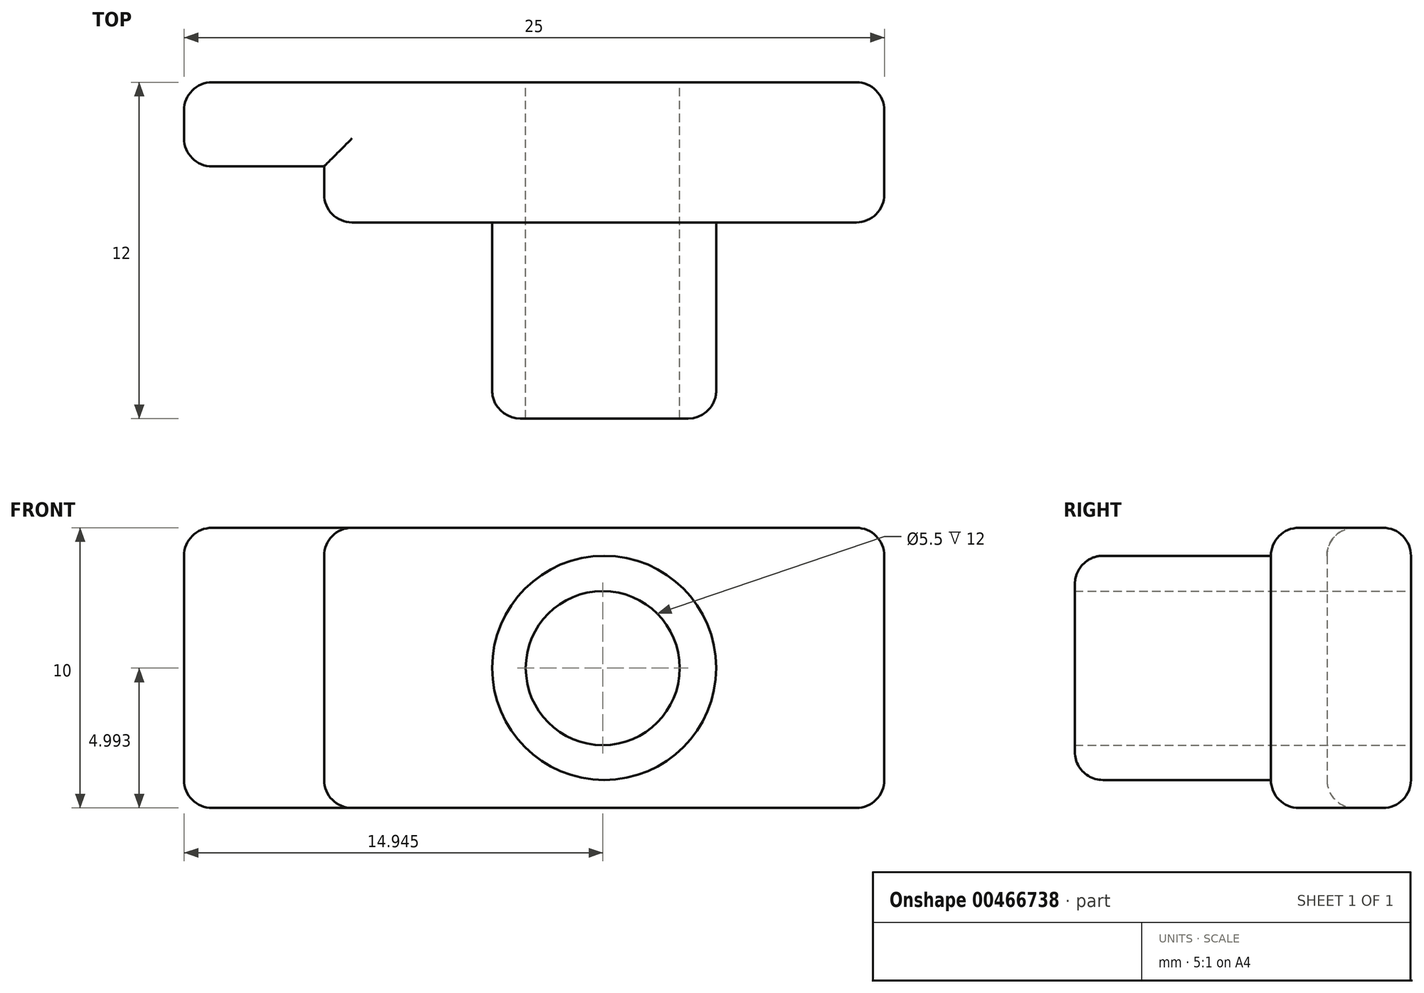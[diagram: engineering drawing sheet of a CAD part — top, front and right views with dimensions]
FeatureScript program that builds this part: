
annotation { "Feature Type Name" : "Feature", "Feature Type Description" : "" }
export const myFeature = defineFeature(function(context is Context, id is Id, definition is map)
    precondition{}
    {
        {
            var Q0;
            Q0=qCreatedBy(makeId("Top.planeOp"),FACE);
            var sketch = newSketch(context, id + "F0", { "sketchPlane" : qUnion([Q0])});
            skLineSegment(sketch, "E0", {"start": v(-34.73, 20.26) * mm, "end": v(-9.73, 20.26) * mm});
            skLineSegment(sketch, "E1", {"start": v(-9.73, 20.26) * mm, "end": v(-9.73, 15.26) * mm});
            skLineSegment(sketch, "E2", {"start": v(-9.73, 15.26) * mm, "end": v(-29.73, 15.26) * mm});
            skLineSegment(sketch, "E3", {"start": v(-29.73, 15.26) * mm, "end": v(-29.73, 17.26) * mm});
            skLineSegment(sketch, "E4", {"start": v(-29.73, 17.26) * mm, "end": v(-34.73, 17.26) * mm});
            skLineSegment(sketch, "E5", {"start": v(-34.73, 17.26) * mm, "end": v(-34.73, 20.26) * mm});
            skSolve(sketch);
        }
        {
            var Q0;
            Q0=makeQuery(id+"F0.imprint","IMPRINT",FACE,{"disambiguationData":[TD([[makeQuery(id+"F0.imprint","IMPRINT",EDGE,{"derivedFrom":sQuery(id+"F0.wireOp",EDGE,"E0")}),-1.0]])]});
            extrude(context, id + "F1", {"entities" : qUnion([Q0]), "depth" : 10 * mm, "offsetDistance" : 25 * mm});
        }
        {
            var Q0;
            Q0=makeQuery(id+"F1.opExtrude","SWEPT_FACE",FACE,{"disambiguationData":[OSD([sQuery(id+"F0.wireOp",EDGE,"E2")])]});
            var sketch = newSketch(context, id + "F2", { "sketchPlane" : qUnion([Q0])});
            skLineSegment(sketch, "E6", {"start": v(-29.73, 10) * mm, "end": v(-9.73, 0) * mm});
            skLineSegment(sketch, "E7", {"start": v(-9.73, 10) * mm, "end": v(-29.73, 0) * mm});
            skPoint(sketch, "E8", {"position": v(-19.73, 5) * mm});
            skCircle(sketch, "E9", {"center": v(-19.73, 5) * mm, "radius": 4 * mm});
            skSolve(sketch);
        }
        {
            var Q0;
            {var subQ0=sQuery(id+"F2.wireOp",EDGE,"E7");var subQ1=sQuery(id+"F2.wireOp",EDGE,"E6");var subQ2=makeQuery(id+"F2.imprint","INTERSECT",VERTEX,{"derivedFrom":[subQ1,subQ0]});Q0=makeQuery(id+"F2.imprint","IMPRINT",FACE,{"disambiguationData":[TD([[makeQuery(id+"F2.imprint","IMPRINT",EDGE,{"disambiguationData":[TD([[subQ2,-1.0]])],"derivedFrom":subQ1}),-1.0]])]});}
            var Q1;
            {var subQ0=sQuery(id+"F2.wireOp",EDGE,"E7");var subQ1=sQuery(id+"F2.wireOp",EDGE,"E6");var subQ2=makeQuery(id+"F2.imprint","INTERSECT",VERTEX,{"derivedFrom":[subQ1,subQ0]});Q1=makeQuery(id+"F2.imprint","IMPRINT",FACE,{"disambiguationData":[TD([[makeQuery(id+"F2.imprint","IMPRINT",EDGE,{"disambiguationData":[TD([[subQ2,-1.0]])],"derivedFrom":subQ1}),1.0]])]});}
            var Q2;
            {var subQ0=sQuery(id+"F2.wireOp",EDGE,"E9");var subQ1=sQuery(id+"F2.wireOp",EDGE,"E6");var subQ2=makeQuery(id+"F2.imprint","INTERSECT",VERTEX,{"disambiguationData":[OD(0.0)],"derivedFrom":[subQ1,subQ0]});Q2=makeQuery(id+"F2.imprint","IMPRINT",FACE,{"disambiguationData":[TD([[makeQuery(id+"F2.imprint","IMPRINT",EDGE,{"disambiguationData":[TD([[subQ2,-1.0]])],"derivedFrom":subQ1}),1.0]])]});}
            var Q3;
            {var subQ0=sQuery(id+"F2.wireOp",EDGE,"E9");var subQ1=sQuery(id+"F2.wireOp",EDGE,"E6");var subQ2=makeQuery(id+"F2.imprint","INTERSECT",VERTEX,{"disambiguationData":[OD(0.0)],"derivedFrom":[subQ1,subQ0]});Q3=makeQuery(id+"F2.imprint","IMPRINT",FACE,{"disambiguationData":[TD([[makeQuery(id+"F2.imprint","IMPRINT",EDGE,{"disambiguationData":[TD([[subQ2,-1.0]])],"derivedFrom":subQ1}),-1.0]])]});}
            extrude(context, id + "F3", {"entities" : qUnion([Q0, Q1, Q2, Q3]), "operationType" : NewBodyOperationType.ADD, "depth" : 7 * mm, "offsetDistance" : 25 * mm});
        }
        {
            var Q0;
            Q0=makeQuery(id+"F1.opExtrude","SWEPT_FACE",FACE,{"disambiguationData":[OSD([sQuery(id+"F0.wireOp",EDGE,"E0")])]});
            var sketch = newSketch(context, id + "F4", { "sketchPlane" : qUnion([Q0])});
            skLineSegment(sketch, "E10", {"start": v(9.73, 10) * mm, "end": v(29.8, 0) * mm});
            skLineSegment(sketch, "E11", {"start": v(9.73, 0) * mm, "end": v(29.87, 10) * mm});
            skPoint(sketch, "E12", {"position": v(19.78, 5) * mm});
            skSolve(sketch);
        }
        {
            var Q0;
            Q0=sQuery(id+"F4.wireOp",VERTEX,"E12");
            var Q1;
            Q1=makeQuery(id+"F1.opExtrude","SWEPT_BODY",BODY,{"disambiguationData":[OSD([sQuery(id+"F0.wireOp",EDGE,"E0"),sQuery(id+"F0.wireOp",EDGE,"E1"),sQuery(id+"F0.wireOp",EDGE,"E2"),sQuery(id+"F0.wireOp",EDGE,"E3"),sQuery(id+"F0.wireOp",EDGE,"E4"),sQuery(id+"F0.wireOp",EDGE,"E5")])]});
            hole(context, id + "F5", {"style" : HoleStyle.SIMPLE, "endStyle" : HoleEndStyle.THROUGH, "standardTappedOrClearance" : lookupTablePath({ "standard" : "ISO", "fit" : "Normal", "size" : "M5", "type" : "Clearance" }), "standardBlindInLast" : lookupTablePath({ "fit" : "Standard", "standard" : "ISO", "size" : "M5", "type" : "Clearance" }), "holeDiameter" : 5.5 * mm, "isTappedThrough" : true, "tappedDepth" : 12 * mm, "tapClearance" : 3, "locations" : qUnion([Q0]), "scope" : qUnion([Q1])});
        }
        {
            var Q0;
            Q0=makeQuery(id+"F1.opExtrude","CAP_EDGE",EDGE,{"disambiguationData":[OSD([sQuery(id+"F0.wireOp",EDGE,"E1")])],"isStart":false});
            var Q1;
            Q1=makeQuery(id+"F1.opExtrude","CAP_EDGE",EDGE,{"disambiguationData":[OSD([sQuery(id+"F0.wireOp",EDGE,"E1")])],"isStart":true});
            var Q2;
            Q2=makeQuery(id+"F1.opExtrude","CAP_EDGE",EDGE,{"disambiguationData":[OSD([sQuery(id+"F0.wireOp",EDGE,"E5")])],"isStart":false});
            var Q3;
            Q3=makeQuery(id+"F1.opExtrude","CAP_EDGE",EDGE,{"disambiguationData":[OSD([sQuery(id+"F0.wireOp",EDGE,"E5")])],"isStart":true});
            var Q4;
            Q4=makeQuery(id+"F1.opExtrude","SWEPT_EDGE",EDGE,{"disambiguationData":[OSD([sQuery(id+"F0.wireOp",EDGE,"E0"),sQuery(id+"F0.wireOp",EDGE,"E5")])]});
            var Q5;
            Q5=makeQuery(id+"F1.opExtrude","SWEPT_EDGE",EDGE,{"disambiguationData":[OSD([sQuery(id+"F0.wireOp",EDGE,"E4"),sQuery(id+"F0.wireOp",EDGE,"E5")])]});
            var Q6;
            Q6=makeQuery(id+"F1.opExtrude","SWEPT_EDGE",EDGE,{"disambiguationData":[OSD([sQuery(id+"F0.wireOp",EDGE,"E0"),sQuery(id+"F0.wireOp",EDGE,"E1")])]});
            var Q7;
            Q7=makeQuery(id+"F1.opExtrude","CAP_EDGE",EDGE,{"disambiguationData":[OSD([sQuery(id+"F0.wireOp",EDGE,"E0")])],"isStart":true});
            var Q8;
            Q8=makeQuery(id+"F1.opExtrude","CAP_EDGE",EDGE,{"disambiguationData":[OSD([sQuery(id+"F0.wireOp",EDGE,"E0")])],"isStart":false});
            var Q9;
            Q9=makeQuery(id+"F1.opExtrude","CAP_EDGE",EDGE,{"disambiguationData":[OSD([sQuery(id+"F0.wireOp",EDGE,"E2")])],"isStart":true});
            var Q10;
            Q10=makeQuery(id+"F1.opExtrude","SWEPT_EDGE",EDGE,{"disambiguationData":[OSD([sQuery(id+"F0.wireOp",EDGE,"E2"),sQuery(id+"F0.wireOp",EDGE,"E3")])]});
            var Q11;
            Q11=makeQuery(id+"F1.opExtrude","CAP_EDGE",EDGE,{"disambiguationData":[OSD([sQuery(id+"F0.wireOp",EDGE,"E4")])],"isStart":true});
            var Q12;
            Q12=makeQuery(id+"F1.opExtrude","CAP_EDGE",EDGE,{"disambiguationData":[OSD([sQuery(id+"F0.wireOp",EDGE,"E2")])],"isStart":false});
            var Q13;
            Q13=makeQuery(id+"F1.opExtrude","CAP_EDGE",EDGE,{"disambiguationData":[OSD([sQuery(id+"F0.wireOp",EDGE,"E4")])],"isStart":false});
            var Q14;
            Q14=makeQuery(id+"F1.opExtrude","SWEPT_EDGE",EDGE,{"disambiguationData":[OSD([sQuery(id+"F0.wireOp",EDGE,"E1"),sQuery(id+"F0.wireOp",EDGE,"E2")])]});
            var Q15;
            Q15=makeQuery(id+"F1.opExtrude","CAP_EDGE",EDGE,{"disambiguationData":[OSD([sQuery(id+"F0.wireOp",EDGE,"E3")])],"isStart":true});
            var Q16;
            Q16=makeQuery(id+"F1.opExtrude","CAP_EDGE",EDGE,{"disambiguationData":[OSD([sQuery(id+"F0.wireOp",EDGE,"E3")])],"isStart":false});
            var Q17;
            Q17=makeQuery(id+"F3.opExtrude","CAP_EDGE",EDGE,{"disambiguationData":[OSD([sQuery(id+"F2.wireOp",EDGE,"E9")])],"isStart":false});
            fillet(context, id + "F6", {"entities" : qUnion([Q0, Q1, Q2, Q3, Q4, Q5, Q6, Q7, Q8, Q9, Q10, Q11, Q12, Q13, Q14, Q15, Q16, Q17]), "radius" : 1 * mm, "tangentPropagation" : true, "allowEdgeOverflow" : false});
        }
    });
